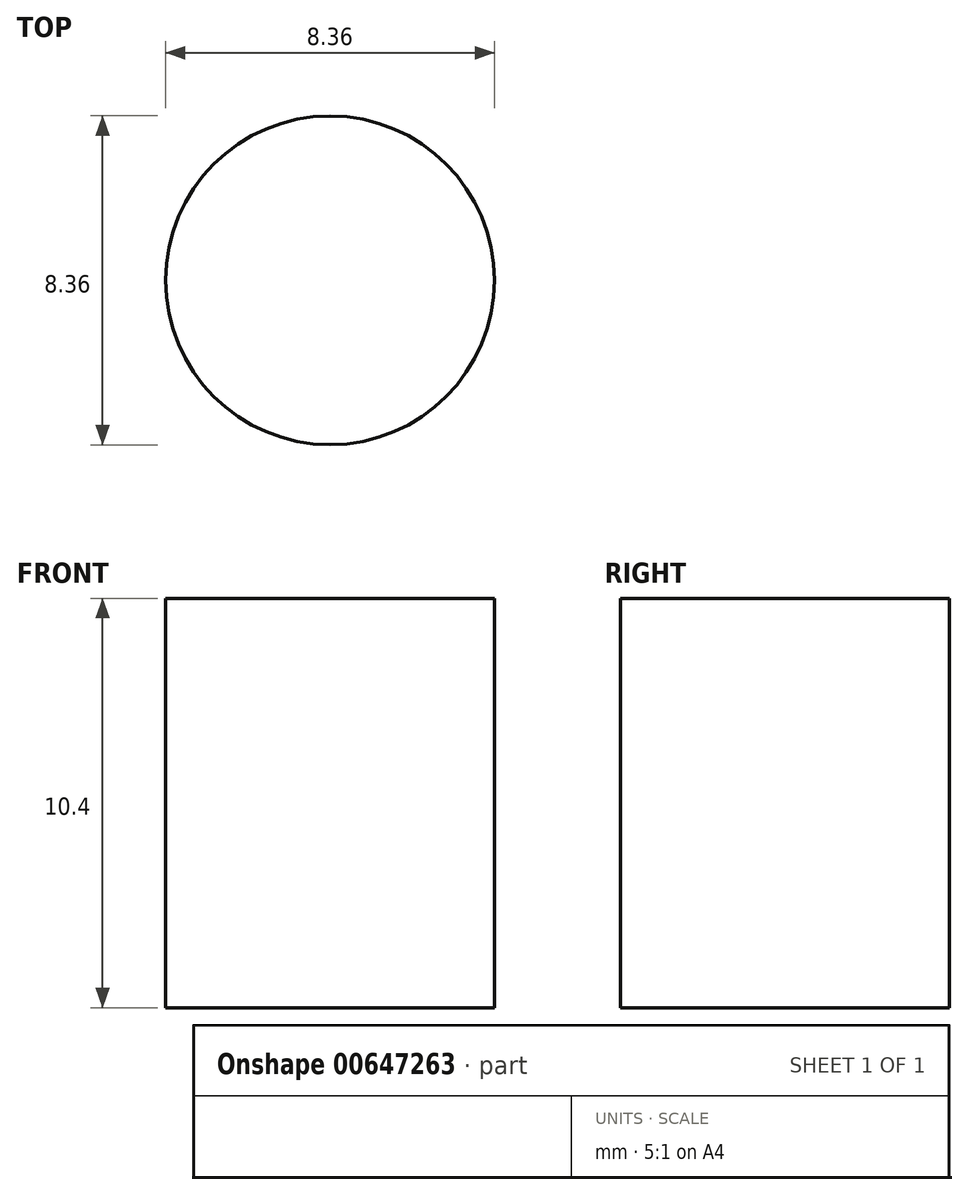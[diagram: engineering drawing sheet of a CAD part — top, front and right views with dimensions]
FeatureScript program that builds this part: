
annotation { "Feature Type Name" : "Feature", "Feature Type Description" : "" }
export const myFeature = defineFeature(function(context is Context, id is Id, definition is map)
    precondition{}
    {
        {
            var Q0;
            Q0=qCreatedBy(makeId("Top.planeOp"),FACE);
            var sketch = newSketch(context, id + "F0", { "sketchPlane" : qUnion([Q0])});
            skCircle(sketch, "E0", {"center": v(0, 0) * mm, "radius": 4.17 * mm});
            skSolve(sketch);
        }
        {
            var Q0;
            Q0 = qSketchRegion(id + "F0", true);
            extrude(context, id + "F1", {"entities" : qUnion([Q0]), "depth" : 10.4 * mm, "offsetDistance" : 25 * mm});
        }
    });
